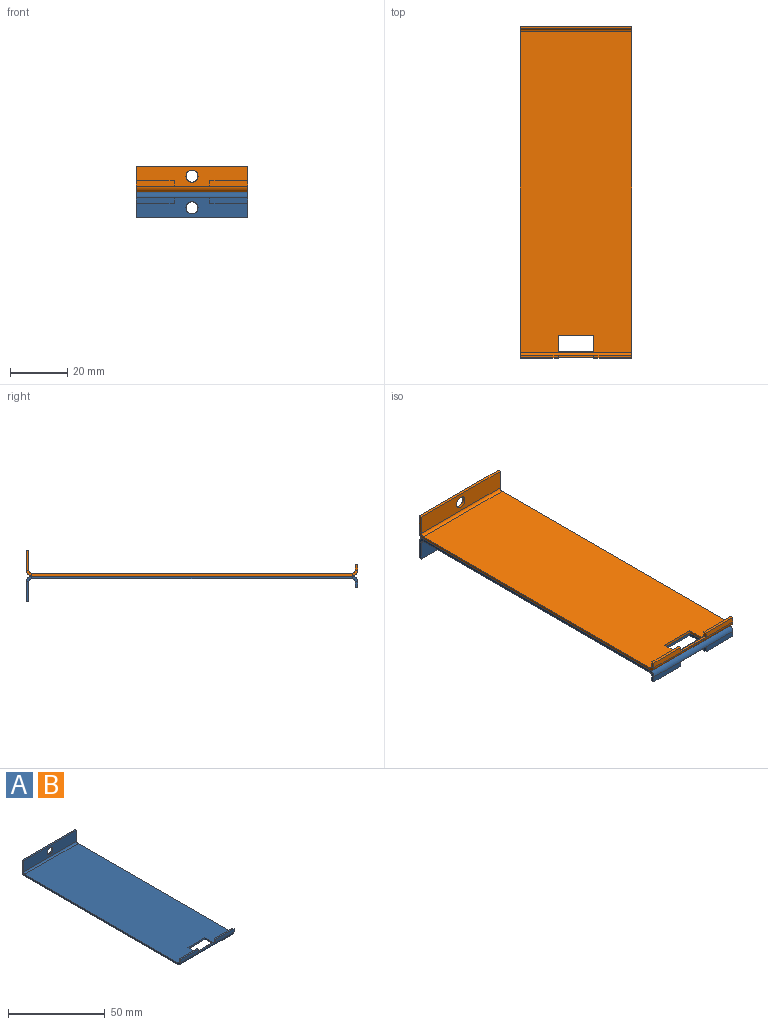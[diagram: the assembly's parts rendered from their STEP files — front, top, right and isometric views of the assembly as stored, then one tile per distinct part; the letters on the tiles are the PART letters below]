
ASSEMBLY  parts=2 mates=1
PART A: 31 faces, bbox 39x116x9 mm
  f0: plane 112x1mm, normal (-1,0,0), area 112mm2, adj f6,f7,f18,f28
  f1: plane 5.75x1mm, normal (1,0,0), area 5.7mm2, adj f2,f4,f6,f7
  f2: plane 12.4x1mm, normal (0,1,0), area 12.4mm2, adj f1,f3,f6,f7
  f3: plane 5.75x1mm, normal (-1,0,0), area 5.7mm2, adj f2,f4,f6,f7
  f4: plane 12.4x1mm, normal (0,-1,0), area 12.4mm2, adj f1,f3,f6,f7
  f5: plane 112x1mm, normal (1,0,0), area 112mm2, adj f6,f7,f17,f27
  f6: plane 112x39mm, normal (0,0,-1), area 4296.7mm2, adj f0,f1,f2,f3,f4,f5,f19,f29
  f7: plane 112x39mm, normal (0,0,1), area 4296.7mm2, adj f0,f1,f2,f3,f4,f5,f20,f30
  f8: plane 12.5x1mm, normal (0,0,1), area 12.5mm2, adj f9,f14,f15,f16
  f9: plane 1.95x1mm, normal (1,0,0), area 2mm2, adj f8,f10,f15,f16
  f10: plane 13.25x1mm, normal (0,0,1), area 13.3mm2, adj f9,f11,f15,f16
  f11: plane 2x1mm, normal (-1,0,0), area 2mm2, adj f10,f15,f16,f18
  f12: plane 2x1mm, normal (1,0,0), area 2mm2, adj f13,f15,f16,f17
  f13: plane 13.25x1mm, normal (0,0,1), area 13.3mm2, adj f12,f14,f15,f16
  f14: plane 1.95x1mm, normal (-1,0,0), area 2mm2, adj f8,f13,f15,f16
  f15: plane 39x2mm, normal (0,-1,0), area 53.6mm2, adj f8,f9,f10,f11,f12,f13,f14,f19
  f16: plane 39x2mm, normal (0,1,0), area 53.6mm2, adj f8,f9,f10,f11,f12,f13,f14,f20
  f17: plane 2x2mm, normal (1,0,0), area 2.4mm2, adj f5,f12,f19,f20
  f18: plane 2x2mm, normal (-1,0,0), area 2.4mm2, adj f0,f11,f19,f20
  f19: cylinder r=2mm len=39mm, axis (1,0,0), area 122.5mm2, adj f6,f15,f17,f18
  f20: cylinder r=1mm len=39mm, axis (1,0,0), area 61.3mm2, adj f7,f16,f17,f18
  f21: plane 39x1mm, normal (0,0,1), area 39mm2, adj f22,f24,f25,f26
  f22: plane 7x1mm, normal (1,0,0), area 7mm2, adj f21,f25,f26,f27
  f23: cylinder r=2.1mm len=4.2mm, axis (0,1,0), area 13.2mm2, adj f25,f26
  f24: plane 7x1mm, normal (-1,0,0), area 7mm2, adj f21,f25,f26,f28
  f25: plane 39x7mm, normal (0,1,0), area 259.1mm2, adj f21,f22,f23,f24,f29
  f26: plane 39x7mm, normal (0,-1,0), area 259.1mm2, adj f21,f22,f23,f24,f30
  f27: plane 2x2mm, normal (1,0,0), area 2.4mm2, adj f5,f22,f29,f30
  f28: plane 2x2mm, normal (-1,0,0), area 2.4mm2, adj f0,f24,f29,f30
  f29: cylinder r=2mm len=39mm, axis (1,0,0), area 122.5mm2, adj f6,f25,f27,f28
  f30: cylinder r=1mm len=39mm, axis (1,0,0), area 61.3mm2, adj f7,f26,f27,f28
PART B: same geometry as A
PLACE A rot(axis=(0,1,0),180deg) t=(-27.45,-5.62,5.6)mm
PLACE B t=(-27.45,-5.62,5.6)mm
MATE fastened A.f6 <-> B.f6  axis (0,0,1) through (-27.45,-4.75,5.6)mm
